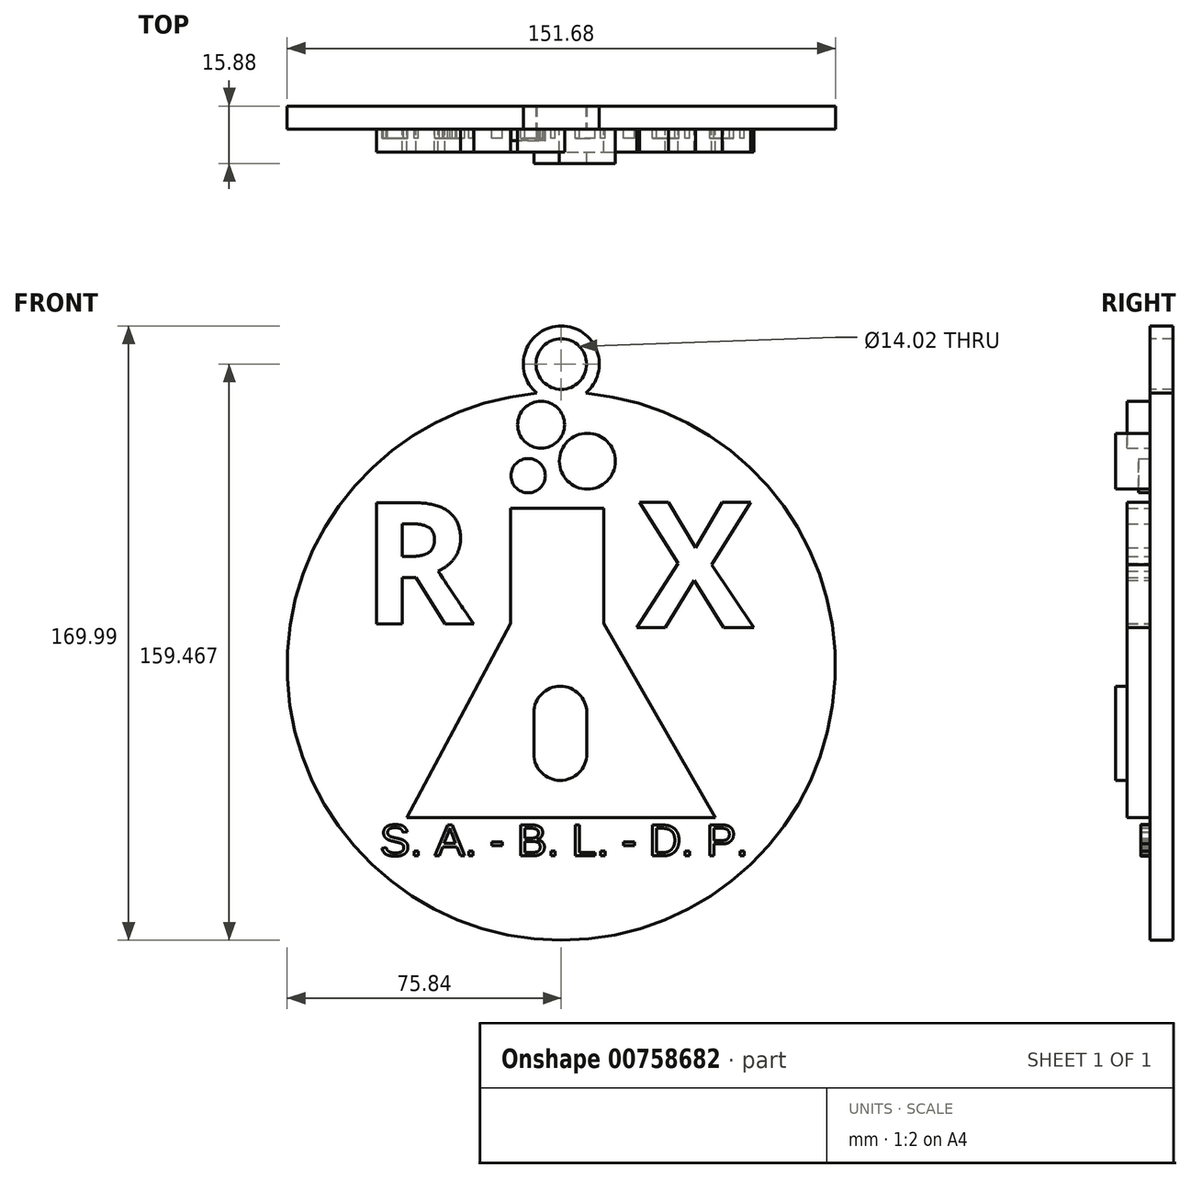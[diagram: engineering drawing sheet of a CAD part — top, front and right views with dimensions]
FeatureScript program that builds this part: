
annotation { "Feature Type Name" : "Feature", "Feature Type Description" : "" }
export const myFeature = defineFeature(function(context is Context, id is Id, definition is map)
    precondition{}
    {
        {
            var Q0;
            Q0=qCreatedBy(makeId("Front.planeOp"),FACE);
            var sketch = newSketch(context, id + "F0", { "sketchPlane" : qUnion([Q0])});
            skCircle(sketch, "E0", {"center": v(0, 0) * mm, "radius": 75.84 * mm});
            skCircle(sketch, "E1", {"center": v(0, 83.63) * mm, "radius": 10.53 * mm});
            skCircle(sketch, "E2", {"center": v(0, 83.63) * mm, "radius": 7 * mm});
            skSolve(sketch);
        }
        {
            var Q0;
            Q0=makeQuery(id+"F0.imprint","IMPRINT",FACE,{"disambiguationData":[TD([[makeQuery(id+"F0.imprint","IMPRINT",EDGE,{"derivedFrom":sQuery(id+"F0.wireOp",EDGE,"E0")}),1.0]])]});
            var sketch = newSketch(context, id + "F1", { "sketchPlane" : qUnion([Q0])});
            skLineSegment(sketch, "E3", {"start": v(-13.98, 43.77) * mm, "end": v(11.82, 43.77) * mm});
            skLineSegment(sketch, "E4", {"start": v(11.82, 43.77) * mm, "end": v(11.82, 11.78) * mm});
            skLineSegment(sketch, "E5", {"start": v(11.82, 11.78) * mm, "end": v(42.57, -41.87) * mm});
            skLineSegment(sketch, "E6", {"start": v(42.57, -41.87) * mm, "end": v(-42.72, -41.87) * mm});
            skLineSegment(sketch, "E7", {"start": v(-42.72, -41.87) * mm, "end": v(-13.98, 11.78) * mm});
            skLineSegment(sketch, "E8", {"start": v(-13.98, 11.78) * mm, "end": v(-13.98, 43.77) * mm});
            skSolve(sketch);
        }
        {
            var Q0;
            Q0=makeQuery(id+"F0.imprint","IMPRINT",FACE,{"disambiguationData":[TD([[makeQuery(id+"F0.imprint","IMPRINT",EDGE,{"derivedFrom":sQuery(id+"F0.wireOp",EDGE,"E0")}),1.0]])]});
            var sketch = newSketch(context, id + "F2", { "sketchPlane" : qUnion([Q0])});
            skLineSegment(sketch, "E9", {"start": v(-4.97, -11.2) * mm, "end": v(-4.97, -21.5) * mm});
            skLineSegment(sketch, "E10", {"start": v(6.9, -11.2) * mm, "end": v(6.9, -21.5) * mm});
            skArc(sketch, "E11", {"start": v(-4.97, -11.2) * mm, "mid": v(0.97, -5.26) * mm, "end": v(6.9, -11.2) * mm});
            skArc(sketch, "E12", {"start": v(-4.97, -21.5) * mm, "mid": v(0.97, -27.45) * mm, "end": v(6.9, -21.5) * mm});
            skLineSegment(sketch, "E13", {"start": v(-4.97, -11.2) * mm, "end": v(6.9, -11.2) * mm});
            skLineSegment(sketch, "E14", {"start": v(-4.97, -21.5) * mm, "end": v(6.9, -21.5) * mm});
            skText(sketch, "E15", { "text": "R", "fontName": "OpenSans-Bold.ttf"});
            skText(sketch, "E16", { "text": "X", "fontName": "OpenSans-Bold.ttf"});
            const initialGuessF2  = {"E15": [-0.05422, 0.00814, 1, 0, 0.03747], "E16": [0.02087, 0.01066, 1, 0, 0.03495]};
            skSetInitialGuess(sketch, initialGuessF2);
            skSolve(sketch);
        }
        {
            var Q0;
            Q0=makeQuery(id+"F0.imprint","IMPRINT",FACE,{"disambiguationData":[TD([[makeQuery(id+"F0.imprint","IMPRINT",EDGE,{"derivedFrom":sQuery(id+"F0.wireOp",EDGE,"E0")}),1.0]])]});
            extrude(context, id + "F3", {"entities" : qUnion([Q0]), "oppositeDirection" : true, "depth" : 5.08 * mm, "offsetDistance" : 25.4 * mm});
        }
        {
            var Q0;
            Q0=makeQuery(id+"F1.imprint","IMPRINT",FACE,{"disambiguationData":[TD([[makeQuery(id+"F1.imprint","IMPRINT",EDGE,{"derivedFrom":sQuery(id+"F1.wireOp",EDGE,"E3")}),-1.0]])]});
            extrude(context, id + "F4", {"entities" : qUnion([Q0]), "operationType" : NewBodyOperationType.ADD, "depth" : 6.35 * mm, "offsetDistance" : 25.4 * mm});
        }
        {
            var Q0;
            Q0=makeQuery(id+"F2.imprint","IMPRINT",FACE,{"disambiguationData":[TD([[makeQuery(id+"F2.imprint","IMPRINT",EDGE,{"derivedFrom":sQuery(id+"F2.wireOp",EDGE,"E16.sketch_text.stroke-0")}),-1.0]])]});
            extrude(context, id + "F5", {"entities" : qUnion([Q0]), "operationType" : NewBodyOperationType.ADD, "depth" : 6.35 * mm, "offsetDistance" : 25.4 * mm});
        }
        {
            var Q0;
            Q0=makeQuery(id+"F4.opExtrude","CAP_FACE",FACE,{"disambiguationData":[OSD([sQuery(id+"F1.wireOp",EDGE,"E3"),sQuery(id+"F1.wireOp",EDGE,"E4"),sQuery(id+"F1.wireOp",EDGE,"E5"),sQuery(id+"F1.wireOp",EDGE,"E6"),sQuery(id+"F1.wireOp",EDGE,"E7"),sQuery(id+"F1.wireOp",EDGE,"E8")])],"isStart":false});
            var sketch = newSketch(context, id + "F6", { "sketchPlane" : qUnion([Q0])});
            skLineSegment(sketch, "E17", {"start": v(-7.59, -12.84) * mm, "end": v(-7.59, -24.29) * mm});
            skLineSegment(sketch, "E18", {"start": v(-7.59, -24.29) * mm, "end": v(7.04, -24.29) * mm});
            skLineSegment(sketch, "E19", {"start": v(7.04, -24.29) * mm, "end": v(7.04, -12.84) * mm});
            skLineSegment(sketch, "E20", {"start": v(7.04, -12.84) * mm, "end": v(-7.59, -12.84) * mm});
            skArc(sketch, "E21", {"start": v(-7.59, -12.84) * mm, "mid": v(-0.28, -5.52) * mm, "end": v(7.04, -12.84) * mm});
            skArc(sketch, "E22", {"start": v(7.04, -24.29) * mm, "mid": v(-0.28, -31.6) * mm, "end": v(-7.59, -24.29) * mm});
            skSolve(sketch);
        }
        {
            var Q0;
            Q0=makeQuery(id+"F3.opExtrude","CAP_FACE",FACE,{"disambiguationData":[OSD([sQuery(id+"F0.wireOp",EDGE,"E0")])],"isStart":true});
            var sketch = newSketch(context, id + "F7", { "sketchPlane" : qUnion([Q0])});
            skText(sketch, "E23", { "text": "R", "fontName": "OpenSans-Bold.ttf"});
            const initialGuessF7  = {"E23": [-0.0553, 0.0117, 1, 0, 0.03387]};
            skSetInitialGuess(sketch, initialGuessF7);
            skSolve(sketch);
        }
        {
            var Q0;
            Q0=makeQuery(id+"F7.imprint","IMPRINT",FACE,{"disambiguationData":[TD([[makeQuery(id+"F7.imprint","IMPRINT",EDGE,{"derivedFrom":sQuery(id+"F7.wireOp",EDGE,"E23.sketch_text.stroke-0")}),-1.0]])]});
            extrude(context, id + "F8", {"entities" : qUnion([Q0]), "operationType" : NewBodyOperationType.ADD, "depth" : 6.35 * mm, "offsetDistance" : 25.4 * mm});
        }
        {
            var Q0;
            {var subQ0=sQuery(id+"F0.wireOp",EDGE,"E0");Q0=makeQuery(id+"F8.boolean.opBoolean","SPLIT",FACE,{"disambiguationData":[TD([makeQuery(id+"F3.opExtrude","SWEPT_FACE",FACE,{"disambiguationData":[OSD([subQ0])]})])],"derivedFrom":makeQuery(id+"F3.opExtrude","CAP_FACE",FACE,{"disambiguationData":[OSD([subQ0])],"isStart":true})});}
            var sketch = newSketch(context, id + "F9", { "sketchPlane" : qUnion([Q0])});
            skCircle(sketch, "E24", {"center": v(-8.47, 52.06) * mm, "radius": 4.59 * mm});
            skCircle(sketch, "E25", {"center": v(12.07, 58.55) * mm, "radius": 6.3 * mm});
            skCircle(sketch, "E26", {"center": v(-5.58, 66.83) * mm, "radius": 6.5 * mm});
            skSolve(sketch);
        }
        {
            var Q0;
            {var subQ0=sQuery(id+"F0.wireOp",EDGE,"E0");Q0=makeQuery(id+"F8.boolean.opBoolean","SPLIT",FACE,{"disambiguationData":[TD([makeQuery(id+"F3.opExtrude","SWEPT_FACE",FACE,{"disambiguationData":[OSD([subQ0])]})])],"derivedFrom":makeQuery(id+"F3.opExtrude","CAP_FACE",FACE,{"disambiguationData":[OSD([subQ0])],"isStart":true})});}
            var sketch = newSketch(context, id + "F10", { "sketchPlane" : qUnion([Q0])});
            skCircle(sketch, "E27", {"center": v(7.23, 56.74) * mm, "radius": 7.74 * mm});
            skSolve(sketch);
        }
        {
            var Q0;
            Q0=makeQuery(id+"F10.imprint","IMPRINT",FACE,{"disambiguationData":[TD([[makeQuery(id+"F10.imprint","IMPRINT",EDGE,{"derivedFrom":sQuery(id+"F10.wireOp",EDGE,"E27")}),1.0]])]});
            extrude(context, id + "F11", {"entities" : qUnion([Q0]), "operationType" : NewBodyOperationType.ADD, "depth" : 9.52 * mm, "offsetDistance" : 25.4 * mm});
        }
        {
            var Q0;
            {var subQ0=sQuery(id+"F0.wireOp",EDGE,"E0");Q0=makeQuery(id+"F8.boolean.opBoolean","SPLIT",FACE,{"disambiguationData":[TD([makeQuery(id+"F3.opExtrude","SWEPT_FACE",FACE,{"disambiguationData":[OSD([subQ0])]})])],"derivedFrom":makeQuery(id+"F3.opExtrude","CAP_FACE",FACE,{"disambiguationData":[OSD([subQ0])],"isStart":true})});}
            var sketch = newSketch(context, id + "F12", { "sketchPlane" : qUnion([Q0])});
            skCircle(sketch, "E28", {"center": v(-9.16, 52.73) * mm, "radius": 4.75 * mm});
            skSolve(sketch);
        }
        {
            var Q0;
            Q0=makeQuery(id+"F9.imprint","IMPRINT",FACE,{"disambiguationData":[TD([[makeQuery(id+"F9.imprint","IMPRINT",EDGE,{"derivedFrom":sQuery(id+"F9.wireOp",EDGE,"E26")}),1.0]])]});
            extrude(context, id + "F13", {"entities" : qUnion([Q0]), "operationType" : NewBodyOperationType.ADD, "depth" : 6.35 * mm, "offsetDistance" : 25.4 * mm});
        }
        {
            var Q0;
            Q0=makeQuery(id+"F12.imprint","IMPRINT",FACE,{"disambiguationData":[TD([[makeQuery(id+"F12.imprint","IMPRINT",EDGE,{"derivedFrom":sQuery(id+"F12.wireOp",EDGE,"E28")}),1.0]])]});
            extrude(context, id + "F14", {"entities" : qUnion([Q0]), "operationType" : NewBodyOperationType.ADD, "depth" : 3.17 * mm, "offsetDistance" : 25.4 * mm});
        }
        {
            var Q0;
            {var subQ0=sQuery(id+"F0.wireOp",EDGE,"E0");Q0=makeQuery(id+"F8.boolean.opBoolean","SPLIT",FACE,{"disambiguationData":[TD([makeQuery(id+"F3.opExtrude","SWEPT_FACE",FACE,{"disambiguationData":[OSD([subQ0])]})])],"derivedFrom":makeQuery(id+"F3.opExtrude","CAP_FACE",FACE,{"disambiguationData":[OSD([subQ0])],"isStart":true})});}
            var sketch = newSketch(context, id + "F15", { "sketchPlane" : qUnion([Q0])});
            skText(sketch, "E29", { "text": "S. A. - B. L. - D. P.", "fontName": "Arimo-Regular.ttf"});
            const initialGuessF15  = {"E29": [-0.05013, -0.05245, 1, 0, 0.00892]};
            skSetInitialGuess(sketch, initialGuessF15);
            skSolve(sketch);
        }
        {
            var Q0;
            Q0 = qSketchRegion(id + "F15", true);
            extrude(context, id + "F16", {"entities" : qUnion([Q0]), "operationType" : NewBodyOperationType.ADD, "depth" : 2.54 * mm, "offsetDistance" : 25.4 * mm});
        }
        {
            var Q0;
            Q0=makeQuery(id+"F6.imprint","IMPRINT",FACE,{"disambiguationData":[TD([[makeQuery(id+"F6.imprint","IMPRINT",EDGE,{"derivedFrom":sQuery(id+"F6.wireOp",EDGE,"E18")}),-1.0]])]});
            var Q1;
            Q1=makeQuery(id+"F6.imprint","IMPRINT",FACE,{"disambiguationData":[TD([[makeQuery(id+"F6.imprint","IMPRINT",EDGE,{"derivedFrom":sQuery(id+"F6.wireOp",EDGE,"E17")}),1.0]])]});
            var Q2;
            Q2=makeQuery(id+"F6.imprint","IMPRINT",FACE,{"disambiguationData":[TD([[makeQuery(id+"F6.imprint","IMPRINT",EDGE,{"derivedFrom":sQuery(id+"F6.wireOp",EDGE,"E20")}),-1.0]])]});
            extrude(context, id + "F17", {"entities" : qUnion([Q0, Q1, Q2]), "operationType" : NewBodyOperationType.ADD, "depth" : 3.17 * mm, "offsetDistance" : 25.4 * mm});
        }
        {
            var Q0;
            Q0 = qSketchRegion(id + "F0", true);
            extrude(context, id + "F18", {"entities" : qUnion([Q0]), "operationType" : NewBodyOperationType.ADD, "oppositeDirection" : true, "depth" : 6.35 * mm, "offsetDistance" : 25.4 * mm});
        }
    });
